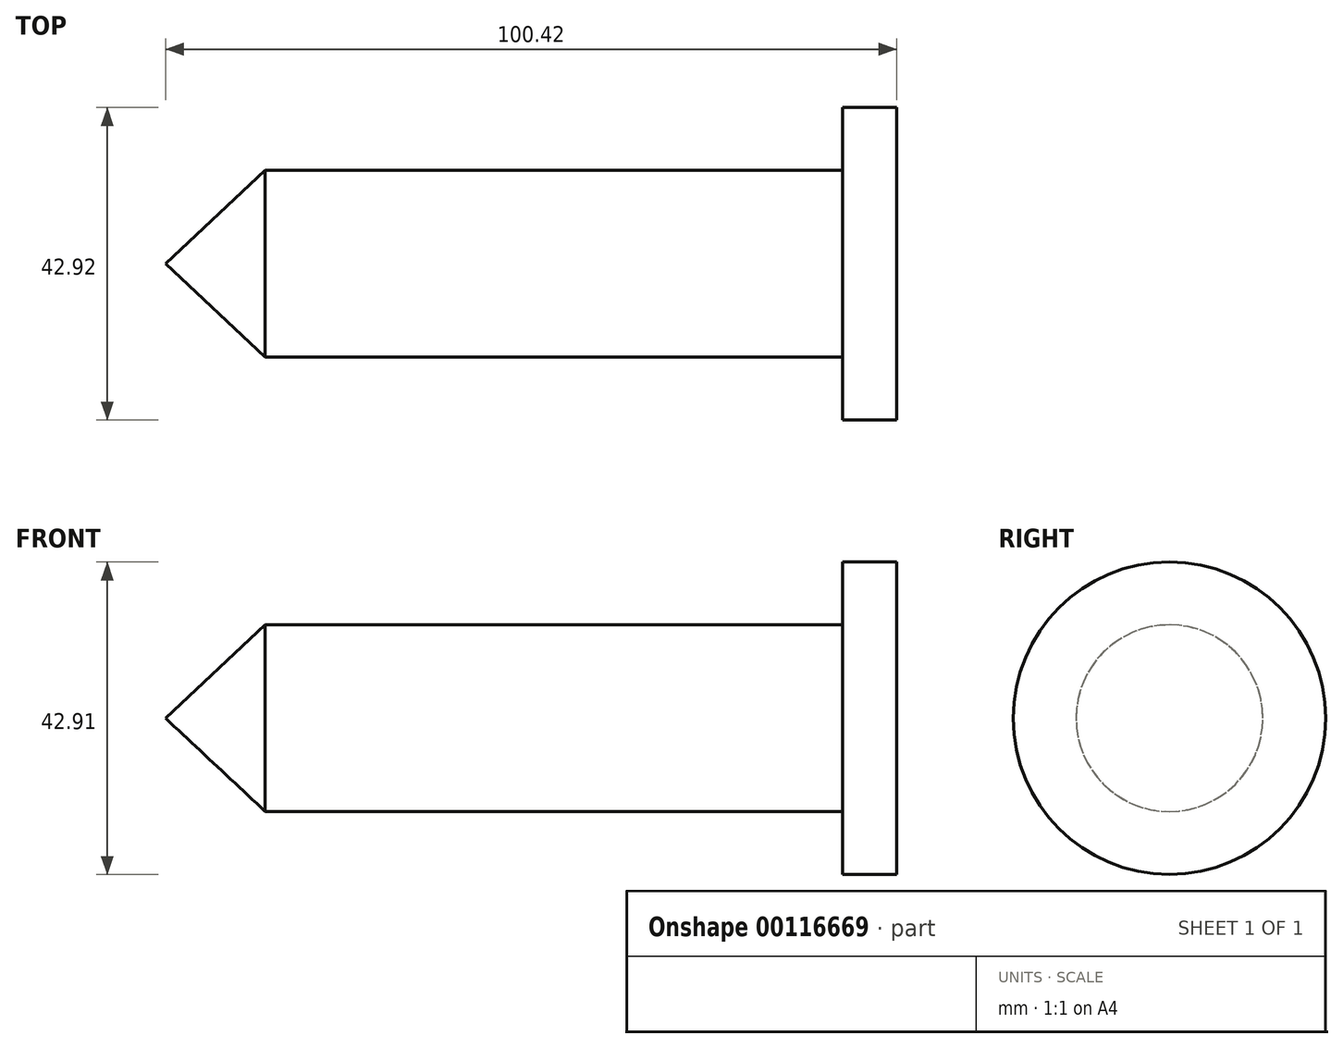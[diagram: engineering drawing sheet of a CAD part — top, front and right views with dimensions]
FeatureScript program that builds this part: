
annotation { "Feature Type Name" : "Feature", "Feature Type Description" : "" }
export const myFeature = defineFeature(function(context is Context, id is Id, definition is map)
    precondition{}
    {
        {
            var Q0;
            Q0=qCreatedBy(makeId("Front.planeOp"),FACE);
            var sketch = newSketch(context, id + "F0", { "sketchPlane" : qUnion([Q0])});
            skLineSegment(sketch, "E0.bottom", {"start": v(-39.63, 6.4) * mm, "end": v(39.63, 6.4) * mm});
            skLineSegment(sketch, "E0.top", {"start": v(-39.63, -6.4) * mm, "end": v(39.63, -6.4) * mm});
            skLineSegment(sketch, "E0.left", {"start": v(-39.63, 6.4) * mm, "end": v(-39.63, -6.4) * mm});
            skLineSegment(sketch, "E0.right", {"start": v(39.63, 6.4) * mm, "end": v(39.63, -6.4) * mm});
            skPoint(sketch, "E0.middle", {"position": v(0, 0) * mm});
            skLineSegment(sketch, "E1", {"start": v(-39.63, -6.4) * mm, "end": v(-53.34, -6.4) * mm});
            skLineSegment(sketch, "E2", {"start": v(-53.34, -6.4) * mm, "end": v(-39.63, 6.4) * mm});
            skLineSegment(sketch, "E3.bottom", {"start": v(39.63, -6.4) * mm, "end": v(47.08, -6.4) * mm});
            skLineSegment(sketch, "E3.top", {"start": v(39.63, 15.05) * mm, "end": v(47.08, 15.05) * mm});
            skLineSegment(sketch, "E3.left", {"start": v(39.63, -6.4) * mm, "end": v(39.63, 15.05) * mm});
            skLineSegment(sketch, "E3.right", {"start": v(47.08, -6.4) * mm, "end": v(47.08, 15.05) * mm});
            skSolve(sketch);
        }
        {
            var Q0;
            Q0 = qSketchRegion(id + "F0", true);
            var Q1;
            Q1=sQuery(id+"F0.wireOp",EDGE,"E0.top");
            revolve(context, id + "F1", {"entities" : qUnion([Q0]), "axis" : qUnion([Q1]), "revolveType" : RevolveType.FULL});
        }
    });
